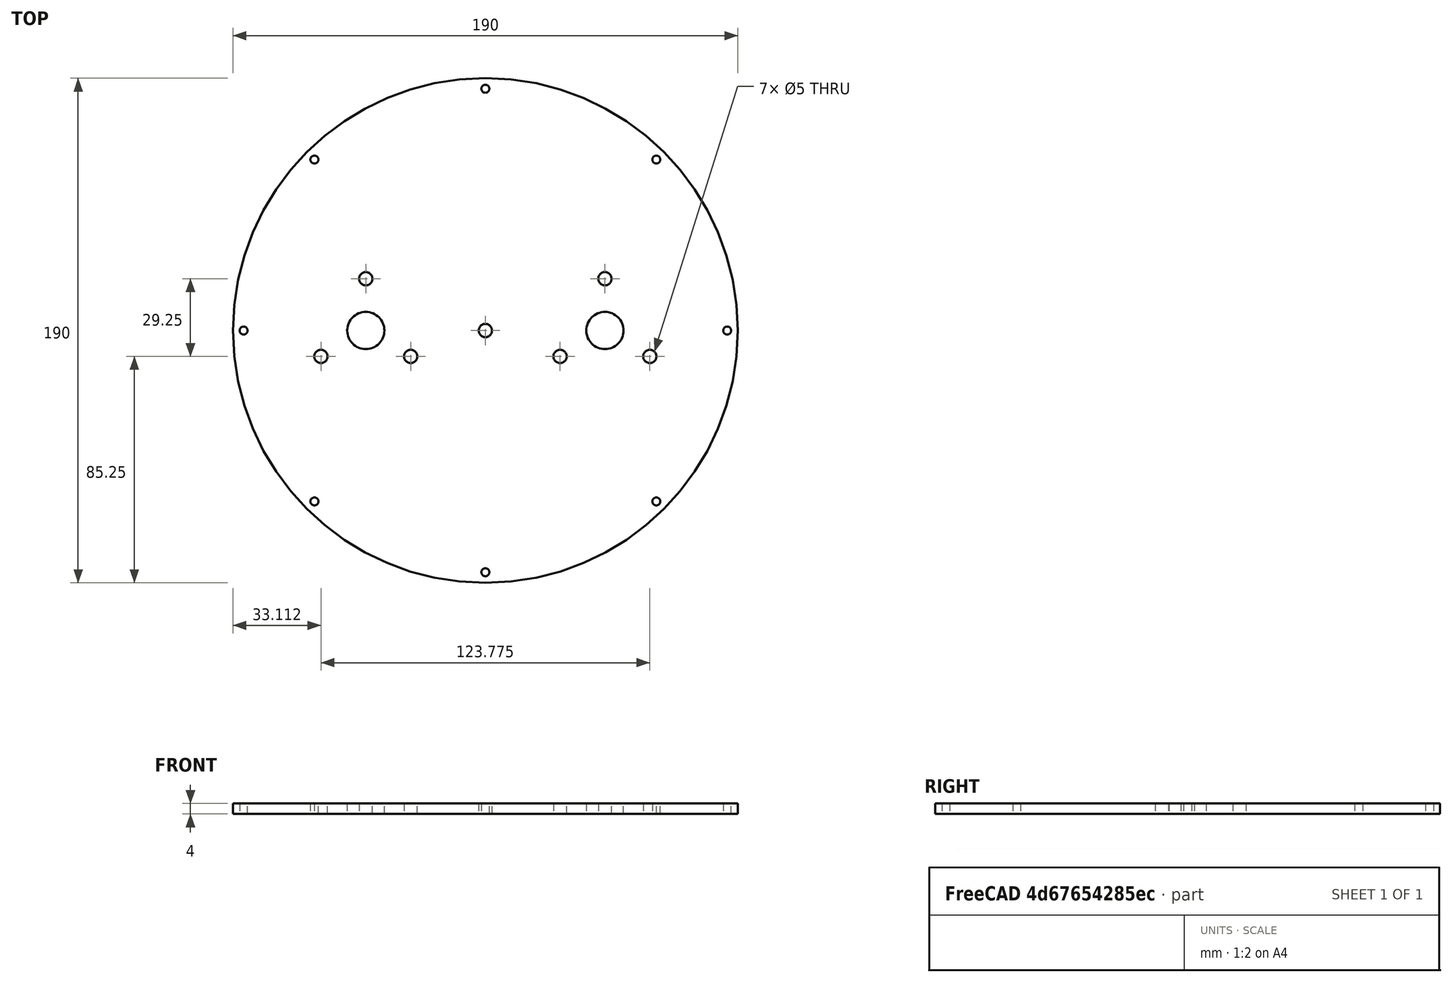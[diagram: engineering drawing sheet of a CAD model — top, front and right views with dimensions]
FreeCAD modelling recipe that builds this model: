
FCSTD DOCUMENT  (FreeCAD 0.19R24276 (Git))
Label: Osnovanie_karuseli
License: All rights reserved
LicenseURL: http://en.wikipedia.org/wiki/All_rights_reserved
objects: Sketcher::SketchObject×1, PartDesign::Pad×1, PartDesign::Body×1
note: 4 computed .brp shape members not serialized (recipe doc carries the construction recipe); baked Part::Feature solids carry a one-line shape summary decoded from their .brp

FEATURE [Sketcher::SketchObject] Sketch
  FullyConstrained = false
  MapMode = 5
  Support = -> [XY_Plane]
  sketch-geometry (35):
    g0: Circle CenterX=-2e-16 CenterY=0 CenterZ=0 NormalX=0 NormalY=0 NormalZ=1 AngleXU=0 Radius=95
    g1: Circle CenterX=-45 CenterY=0 CenterZ=0 NormalX=0 NormalY=0 NormalZ=1 AngleXU=0 Radius=7
    g2: Circle CenterX=45 CenterY=0 CenterZ=0 NormalX=0 NormalY=0 NormalZ=1 AngleXU=0 Radius=7
    g3: LineSegment StartX=-2e-16 StartY=0 StartZ=0 EndX=64.3467 EndY=64.3467 EndZ=0
    g4: LineSegment StartX=-2e-16 StartY=0 StartZ=0 EndX=-64.3467 EndY=64.3467 EndZ=0
    g5: LineSegment StartX=-2e-16 StartY=0 StartZ=0 EndX=-64.3467 EndY=-64.3467 EndZ=0
    g6: LineSegment StartX=-2e-16 StartY=0 StartZ=0 EndX=64.3467 EndY=-64.3467 EndZ=0
    g7: Circle CenterX=-2e-16 CenterY=0 CenterZ=0 NormalX=0 NormalY=0 NormalZ=1 AngleXU=0 Radius=91
    g8: Circle CenterX=64.3467 CenterY=64.3467 CenterZ=0 NormalX=0 NormalY=0 NormalZ=1 AngleXU=0 Radius=1.5
    g9: Circle CenterX=-64.3467 CenterY=64.3467 CenterZ=0 NormalX=0 NormalY=0 NormalZ=1 AngleXU=0 Radius=1.5
    g10: Circle CenterX=-64.3467 CenterY=-64.3467 CenterZ=0 NormalX=0 NormalY=0 NormalZ=1 AngleXU=0 Radius=1.5
    g11: Circle CenterX=64.3467 CenterY=-64.3467 CenterZ=0 NormalX=0 NormalY=0 NormalZ=1 AngleXU=0 Radius=1.5
    g12: LineSegment StartX=-45 StartY=19.5 StartZ=0 EndX=-61.8875 EndY=-9.75 EndZ=0
    g13: LineSegment StartX=-61.8875 StartY=-9.75 StartZ=0 EndX=-28.1125 EndY=-9.75 EndZ=0
    g14: LineSegment StartX=-28.1125 StartY=-9.75 StartZ=0 EndX=-45 EndY=19.5 EndZ=0
    g15: Circle CenterX=-45 CenterY=0 CenterZ=0 NormalX=0 NormalY=0 NormalZ=1 AngleXU=0 Radius=19.5
    g16: LineSegment StartX=45 StartY=19.5 StartZ=0 EndX=28.1125 EndY=-9.75 EndZ=0
    g17: LineSegment StartX=28.1125 StartY=-9.75 StartZ=0 EndX=61.8875 EndY=-9.75 EndZ=0
    g18: LineSegment StartX=61.8875 StartY=-9.75 StartZ=0 EndX=45 EndY=19.5 EndZ=0
    g19: Circle CenterX=45 CenterY=0 CenterZ=0 NormalX=0 NormalY=0 NormalZ=1 AngleXU=0 Radius=19.5
    g20: Circle CenterX=-45 CenterY=19.5 CenterZ=0 NormalX=0 NormalY=0 NormalZ=1 AngleXU=0 Radius=2.5
    g21: Circle CenterX=-28.1125 CenterY=-9.75 CenterZ=0 NormalX=0 NormalY=0 NormalZ=1 AngleXU=0 Radius=2.5
    g22: Circle CenterX=-61.8875 CenterY=-9.75 CenterZ=0 NormalX=0 NormalY=0 NormalZ=1 AngleXU=0 Radius=2.5
    g23: Circle CenterX=45 CenterY=19.5 CenterZ=0 NormalX=0 NormalY=0 NormalZ=1 AngleXU=0 Radius=2.5
    g24: Circle CenterX=28.1125 CenterY=-9.75 CenterZ=0 NormalX=0 NormalY=0 NormalZ=1 AngleXU=0 Radius=2.5
    g25: Circle CenterX=61.8875 CenterY=-9.75 CenterZ=0 NormalX=0 NormalY=0 NormalZ=1 AngleXU=0 Radius=2.5
    g26: Circle CenterX=-2e-16 CenterY=0 CenterZ=0 NormalX=0 NormalY=0 NormalZ=1 AngleXU=0 Radius=2.5
    g27: LineSegment StartX=-2e-16 StartY=0 StartZ=0 EndX=91 EndY=0 EndZ=0
    g28: Circle CenterX=91 CenterY=0 CenterZ=0 NormalX=0 NormalY=0 NormalZ=1 AngleXU=0 Radius=1.5
    g29: Circle CenterX=-91 CenterY=0 CenterZ=0 NormalX=0 NormalY=0 NormalZ=1 AngleXU=0 Radius=1.5
    g30: LineSegment StartX=2e-16 StartY=0 StartZ=0 EndX=-91 EndY=0 EndZ=0
    g31: LineSegment StartX=-2e-16 StartY=0 StartZ=0 EndX=0 EndY=91 EndZ=0
    g32: Circle CenterX=0 CenterY=91 CenterZ=0 NormalX=0 NormalY=0 NormalZ=1 AngleXU=0 Radius=1.5
    g33: LineSegment StartX=-2e-16 StartY=0 StartZ=0 EndX=0 EndY=-91 EndZ=0
    g34: Circle CenterX=0 CenterY=-91 CenterZ=0 NormalX=0 NormalY=0 NormalZ=1 AngleXU=0 Radius=1.5
  constraints (75):
    c: Coincident(g0,g-1)
    c: Diameter(g0) = 190
    c: PointOnObject(g1,g-1)
    c: PointOnObject(g2,g-1)
    c: Diameter(g2) = 14
    c: Equal(g2,g1)
    c: DistanceX(g0,g2) = 45
    c: DistanceX(g1,g0) = 45
    c: Coincident(g3,g0)
    c: Coincident(g4,g0)
    c: Coincident(g5,g0)
    c: Coincident(g6,g0)
    c: Parallel(g3,g5)
    c: Parallel(g4,g6)
    c: Perpendicular(g3,g4)
    c: Angle(g-1,g3) = 0.785398
    c: Coincident(g7,g0)
    c: Diameter(g7) = 182
    c: PointOnObject(g3,g7)
    c: PointOnObject(g4,g7)
    c: PointOnObject(g5,g7)
    c: PointOnObject(g6,g7)
    c: Coincident(g8,g3)
    c: Coincident(g9,g4)
    c: Coincident(g10,g5)
    c: Coincident(g11,g6)
    c: Diameter(g8) = 3
    c: Equal(g8,g9)
    c: Equal(g8,g10)
    c: Equal(g8,g11)
    c: Coincident(g12,g13)
    c: Coincident(g13,g14)
    c: Coincident(g14,g12)
    c: Equal(g12,g13)
    c: Equal(g12,g14)
    c: PointOnObject(g12,g15)
    c: PointOnObject(g13,g15)
    c: PointOnObject(g14,g15)
    c: Coincident(g15,g1)
    c: Coincident(g16,g17)
    c: Coincident(g17,g18)
    c: Coincident(g18,g16)
    c: Equal(g16,g17)
    c: Equal(g16,g18)
    c: PointOnObject(g16,g19)
    c: PointOnObject(g17,g19)
    c: PointOnObject(g18,g19)
    c: Coincident(g19,g2)
    c: Horizontal(g13)
    c: Horizontal(g17)
    c: Diameter(g15) = 39
    c: Diameter(g19) = 39
    c: Coincident(g20,g12)
    c: Coincident(g21,g13)
    c: Coincident(g22,g12)
    c: Coincident(g23,g16)
    c: Coincident(g24,g16)
    c: Coincident(g25,g17)
    c: Diameter(g20) = 5
    c: Equal(g20, g21-g25) x5
    c: Coincident(g26,g0)
    c: Diameter(g26) = 5
    c: Coincident(g27,g0)
    c: Horizontal(g27)
    c: PointOnObject(g27,g7)
    c: Coincident(g28,g27)
    c: Diameter(g28) = 3
    c: Horizontal(g30)
    c: Coincident(g29,g30)
    c: Diameter(g29) = 3
    c: Coincident(g31,g0)
    c: PointOnObject(g31,g7)
    c: Coincident(g32,g31)
    c: Equal(g8,g32)
    c: Coincident(g34,g33)
FEATURE [PartDesign::Pad] Pad
  Direction = (1,1,1)
  Length = 4
  Length2 = 100
  Profile = -> Sketch
  Type = 0
FEATURE [PartDesign::Body] Body
  Group = -> [Sketch,Pad]
  Origin = -> Origin
  Tip = -> Pad
